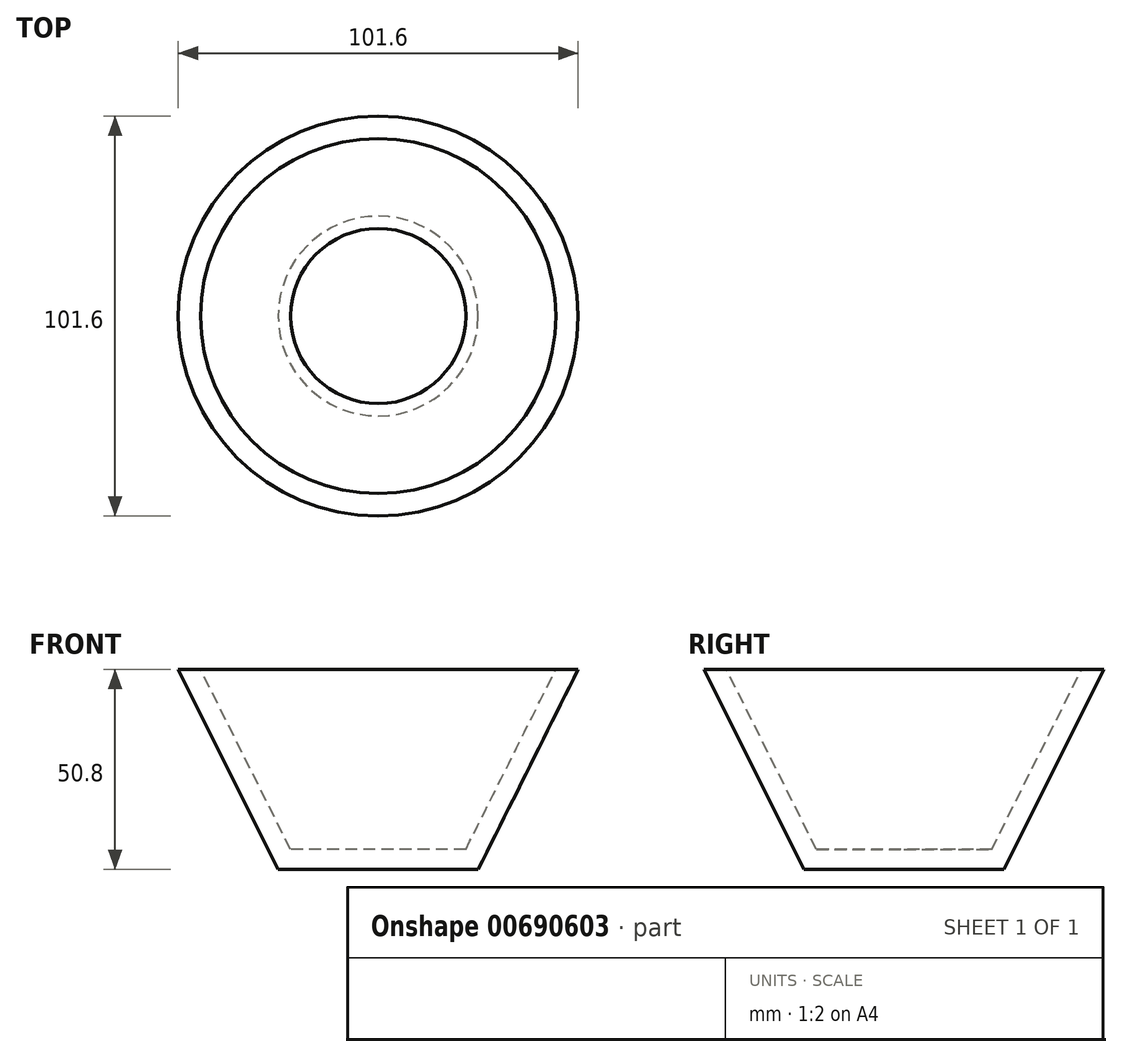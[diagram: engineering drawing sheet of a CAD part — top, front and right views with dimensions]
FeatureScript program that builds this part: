
annotation { "Feature Type Name" : "Feature", "Feature Type Description" : "" }
export const myFeature = defineFeature(function(context is Context, id is Id, definition is map)
    precondition{}
    {
        {
            var Q0;
            Q0=qCreatedBy(makeId("Front.planeOp"),FACE);
            var sketch = newSketch(context, id + "F0", { "sketchPlane" : qUnion([Q0])});
            skLineSegment(sketch, "E0", {"start": v(0, 0) * mm, "end": v(0, -50.8) * mm, "construction": true});
            skLineSegment(sketch, "E1", {"start": v(0, -50.8) * mm, "end": v(25.4, -50.8) * mm});
            skLineSegment(sketch, "E2", {"start": v(25.4, -50.8) * mm, "end": v(50.8, 0) * mm});
            skLineSegment(sketch, "E3.0", {"start": v(22.26, -45.72) * mm, "end": v(45.12, 0) * mm});
            skLineSegment(sketch, "E3.1", {"start": v(0, -45.72) * mm, "end": v(22.26, -45.72) * mm});
            skLineSegment(sketch, "E4", {"start": v(45.12, 0) * mm, "end": v(50.8, 0) * mm});
            skLineSegment(sketch, "E5", {"start": v(0, -45.72) * mm, "end": v(0, -50.8) * mm});
            skSolve(sketch);
        }
        {
            var Q0;
            Q0=makeQuery(id+"F0.imprint","IMPRINT",FACE,{"disambiguationData":[TD([[makeQuery(id+"F0.imprint","IMPRINT",EDGE,{"derivedFrom":sQuery(id+"F0.wireOp",EDGE,"E1")}),1.0]])]});
            var Q1;
            Q1=sQuery(id+"F0.wireOp",EDGE,"E0");
            revolve(context, id + "F1", {"entities" : qUnion([Q0]), "axis" : qUnion([Q1]), "revolveType" : RevolveType.FULL});
        }
    });
